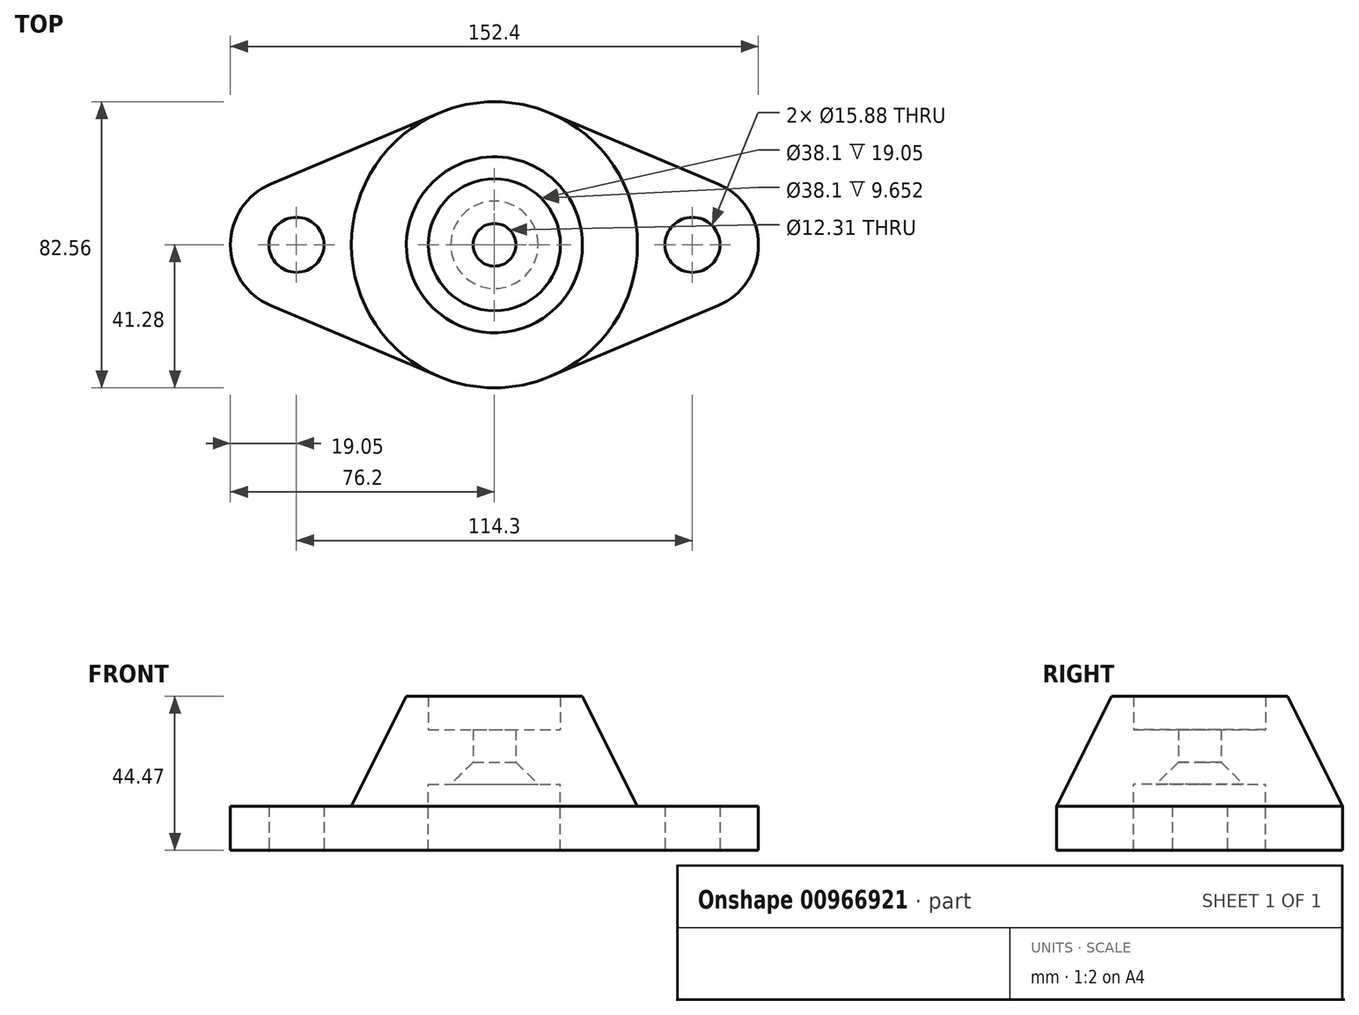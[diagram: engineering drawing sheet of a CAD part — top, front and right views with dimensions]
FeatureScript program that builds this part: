
annotation { "Feature Type Name" : "Feature", "Feature Type Description" : "" }
export const myFeature = defineFeature(function(context is Context, id is Id, definition is map)
    precondition{}
    {
        {
            var Q0;
            Q0=qCreatedBy(makeId("Top.planeOp"),FACE);
            var sketch = newSketch(context, id + "F0", { "sketchPlane" : qUnion([Q0])});
            skLineSegment(sketch, "E0", {"start": v(-94.86, 0) * mm, "end": v(110.11, 0) * mm, "construction": true});
            skLineSegment(sketch, "E1", {"start": v(0, 99.4) * mm, "end": v(0, -94.24) * mm, "construction": true});
            skArc(sketch, "E2", {"start": v(-64.56, 17.55) * mm, "mid": v(-76.2, 0) * mm, "end": v(-64.56, -17.55) * mm});
            skArc(sketch, "E3", {"start": v(64.56, -17.55) * mm, "mid": v(76.2, 0) * mm, "end": v(64.56, 17.55) * mm});
            skCircle(sketch, "E4", {"center": v(0, 0) * mm, "radius": 41.28 * mm});
            skLineSegment(sketch, "E5", {"start": v(-64.56, 17.55) * mm, "end": v(-16.05, 38.03) * mm});
            skLineSegment(sketch, "E6.MirrorCS", {"start": v(-64.56, -17.55) * mm, "end": v(-16.05, -38.03) * mm});
            skLineSegment(sketch, "E7.MirrorCS", {"start": v(64.56, 17.55) * mm, "end": v(16.05, 38.03) * mm});
            skLineSegment(sketch, "E8.MirrorCS", {"start": v(64.56, -17.55) * mm, "end": v(16.05, -38.03) * mm});
            skCircle(sketch, "E9", {"center": v(-57.15, 0) * mm, "radius": 7.94 * mm});
            skCircle(sketch, "E10.MirrorC", {"center": v(57.15, 0) * mm, "radius": 7.94 * mm});
            skSolve(sketch);
        }
        {
            var Q0;
            Q0 = qSketchRegion(id + "F0", true);
            extrude(context, id + "F1", {"entities" : qUnion([Q0]), "depth" : 12.7 * mm, "offsetDistance" : 25.4 * mm});
        }
        {
            var Q0;
            Q0=makeQuery(id+"F1.opExtrude","CAP_FACE",FACE,{"disambiguationData":[OSD([sQuery(id+"F0.wireOp",EDGE,"E2"),sQuery(id+"F0.wireOp",EDGE,"E3"),sQuery(id+"F0.wireOp",EDGE,"E4"),sQuery(id+"F0.wireOp",EDGE,"E5"),sQuery(id+"F0.wireOp",EDGE,"E6.MirrorCS"),sQuery(id+"F0.wireOp",EDGE,"E7.MirrorCS"),sQuery(id+"F0.wireOp",EDGE,"E8.MirrorCS"),sQuery(id+"F0.wireOp",EDGE,"E9"),sQuery(id+"F0.wireOp",EDGE,"E10.MirrorC")])],"isStart":false});
            var sketch = newSketch(context, id + "F2", { "sketchPlane" : qUnion([Q0])});
            skCircle(sketch, "E11", {"center": v(0, 0) * mm, "radius": 41.22 * mm});
            skSolve(sketch);
        }
        {
            var Q0;
            Q0=qCreatedBy(makeId("Front.planeOp"),FACE);
            var sketch = newSketch(context, id + "F3", { "sketchPlane" : qUnion([Q0])});
            skLineSegment(sketch, "E12", {"start": v(0, 73) * mm, "end": v(0, -14.44) * mm, "construction": true});
            skSolve(sketch);
        }
        {
            var Q0;
            Q0=makeQuery(id+"F2.imprint","IMPRINT",FACE,{"disambiguationData":[TD([[makeQuery(id+"F2.imprint","IMPRINT",EDGE,{"derivedFrom":sQuery(id+"F2.wireOp",EDGE,"E11")}),-1.0]])]});
            var sketch = newSketch(context, id + "F4", { "sketchPlane" : qUnion([Q0])});
            skCircle(sketch, "E13", {"center": v(0, 0) * mm, "radius": 19.05 * mm});
            skSolve(sketch);
        }
        {
            var Q0;
            Q0 = qSketchRegion(id + "F4", true);
            extrude(context, id + "F5", {"entities" : qUnion([Q0]), "operationType" : NewBodyOperationType.REMOVE, "endBound" : BoundingType.THROUGH_ALL, "oppositeDirection" : true, "depth" : 25.4 * mm, "offsetDistance" : 25.4 * mm});
        }
        {
            var Q0;
            Q0=qCreatedBy(makeId("Right.planeOp"),FACE);
            var sketch = newSketch(context, id + "F6", { "sketchPlane" : qUnion([Q0])});
            skLineSegment(sketch, "E14", {"start": v(-25.4, 44.47) * mm, "end": v(0, 44.47) * mm});
            skLineSegment(sketch, "E15", {"start": v(-41.28, 12.7) * mm, "end": v(0, 12.7) * mm});
            skLineSegment(sketch, "E16", {"start": v(-25.4, 44.47) * mm, "end": v(-41.28, 12.7) * mm});
            skLineSegment(sketch, "E17", {"start": v(0, 44.47) * mm, "end": v(0, 12.7) * mm});
            skPoint(sketch, "E18.orphan", {"position": v(25.4, 44.47) * mm});
            skPoint(sketch, "E19.orphan", {"position": v(41.28, 12.7) * mm});
            skSolve(sketch);
        }
        {
            var Q0;
            Q0 = qSketchRegion(id + "F6", true);
            var Q1;
            Q1=sQuery(id+"F6.wireOp",EDGE,"E17");
            revolve(context, id + "F7", {"operationType" : NewBodyOperationType.ADD, "surfaceOperationType" : NewSurfaceOperationType.NEW, "entities" : qUnion([Q0]), "axis" : qUnion([Q1]), "revolveType" : RevolveType.FULL});
        }
        {
            var Q0;
            Q0=qCreatedBy(makeId("Front.planeOp"),FACE);
            var sketch = newSketch(context, id + "F8", { "sketchPlane" : qUnion([Q0])});
            skLineSegment(sketch, "E20", {"start": v(0, 44.47) * mm, "end": v(-19.05, 44.47) * mm});
            skLineSegment(sketch, "E21", {"start": v(-19.05, 44.47) * mm, "end": v(-19.05, 34.82) * mm});
            skLineSegment(sketch, "E22", {"start": v(-19.05, 34.82) * mm, "end": v(-6.16, 34.82) * mm});
            skLineSegment(sketch, "E23", {"start": v(-6.16, 34.82) * mm, "end": v(-6.16, 25.4) * mm});
            skLineSegment(sketch, "E24", {"start": v(-12.6, 19.05) * mm, "end": v(-19.05, 19.05) * mm});
            skLineSegment(sketch, "E25", {"start": v(-19.05, 19.05) * mm, "end": v(-19.05, 12.7) * mm});
            skLineSegment(sketch, "E26", {"start": v(-19.05, 12.7) * mm, "end": v(0, 12.7) * mm});
            skLineSegment(sketch, "E27", {"start": v(0, 44.47) * mm, "end": v(0, 12.7) * mm});
            skLineSegment(sketch, "E28", {"start": v(-6.16, 25.4) * mm, "end": v(-12.6, 19.05) * mm});
            skPoint(sketch, "E29.orphan", {"position": v(-6.16, 19.05) * mm});
            skSolve(sketch);
        }
        {
            var Q0;
            Q0 = qSketchRegion(id + "F8", true);
            var Q1;
            Q1=sQuery(id+"F8.wireOp",EDGE,"E27");
            revolve(context, id + "F9", {"operationType" : NewBodyOperationType.REMOVE, "surfaceOperationType" : NewSurfaceOperationType.NEW, "entities" : qUnion([Q0]), "axis" : qUnion([Q1]), "revolveType" : RevolveType.FULL, "oppositeDirection" : true});
        }
        {
            var Q0;
            Q0 = qSketchRegion(id + "F8", true);
            var Q1;
            Q1=sQuery(id+"F3.wireOp",EDGE,"E12");
            revolve(context, id + "F10", {"operationType" : NewBodyOperationType.REMOVE, "surfaceOperationType" : NewSurfaceOperationType.NEW, "entities" : qUnion([Q0]), "axis" : qUnion([Q1]), "revolveType" : RevolveType.FULL, "oppositeDirection" : true});
        }
    });
